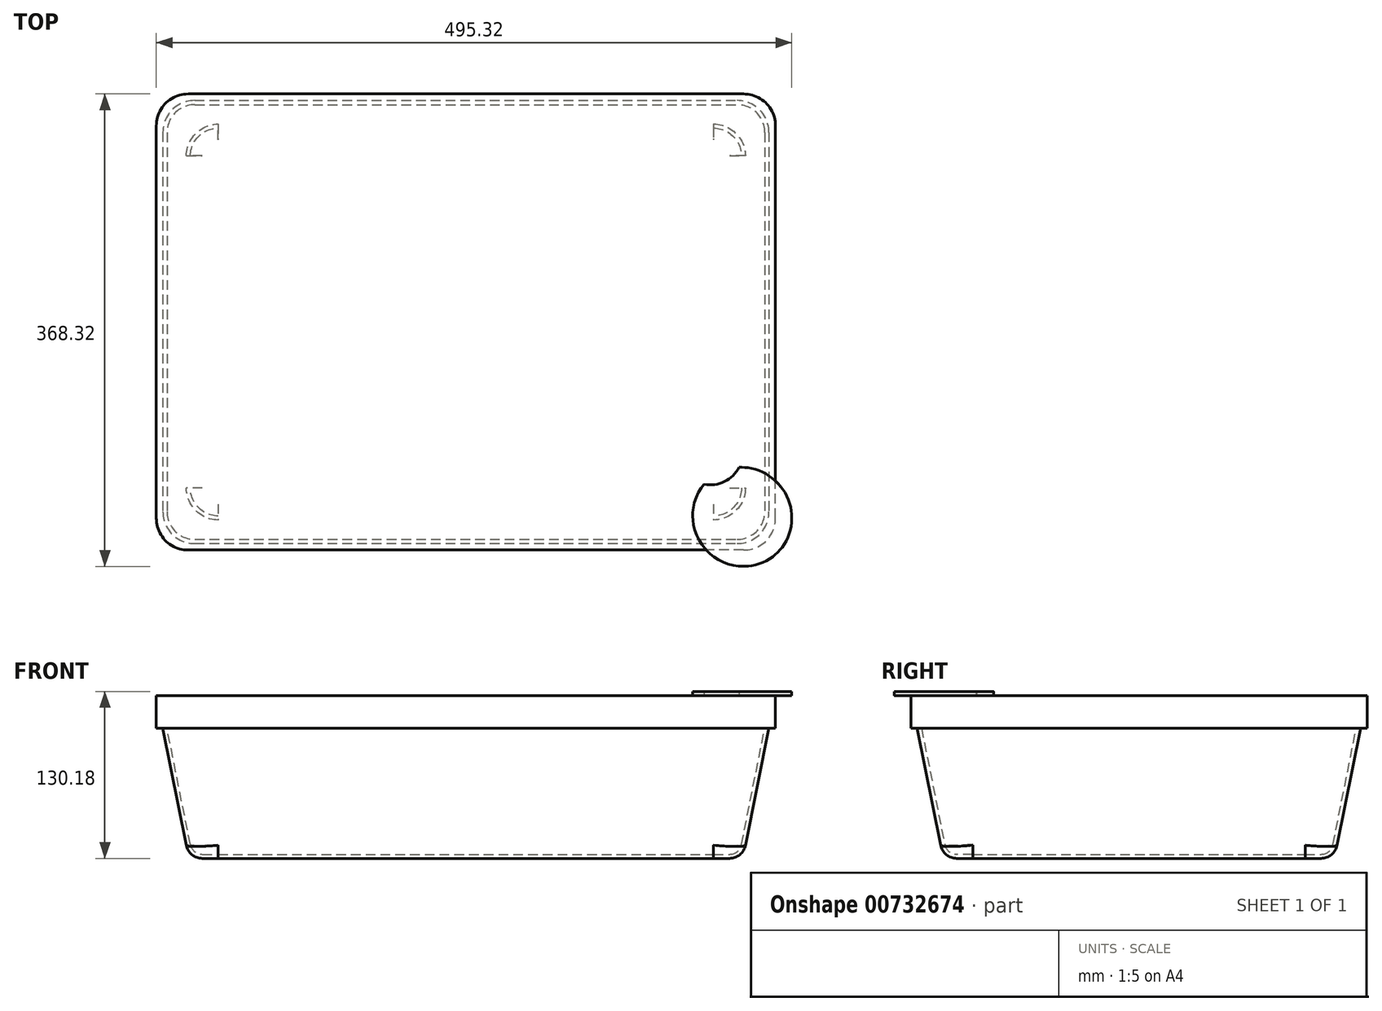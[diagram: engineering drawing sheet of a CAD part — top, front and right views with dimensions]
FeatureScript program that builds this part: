
annotation { "Feature Type Name" : "Feature", "Feature Type Description" : "" }
export const myFeature = defineFeature(function(context is Context, id is Id, definition is map)
    precondition{}
    {
        {
            var Q0;
            Q0=qCreatedBy(makeId("Top.planeOp"),FACE);
            var sketch = newSketch(context, id + "F0", { "sketchPlane" : qUnion([Q0])});
            skLineSegment(sketch, "E0.bottom", {"start": v(-241.3, 177.8) * mm, "end": v(241.3, 177.8) * mm});
            skLineSegment(sketch, "E0.top", {"start": v(-241.3, -177.8) * mm, "end": v(241.3, -177.8) * mm});
            skLineSegment(sketch, "E0.left", {"start": v(-241.3, 177.8) * mm, "end": v(-241.3, -177.8) * mm});
            skLineSegment(sketch, "E0.right", {"start": v(241.3, 177.8) * mm, "end": v(241.3, -177.8) * mm});
            skPoint(sketch, "E0.middle", {"position": v(0, 0) * mm});
            skSolve(sketch);
        }
        {
            var Q0;
            Q0=qCreatedBy(makeId("Top.planeOp"),FACE);
            cPlane(context, id + "F1", {"entities" : qUnion([Q0]), "cplaneType" : CPlaneType.OFFSET, "offset" : 127 * mm, "oppositeDirection" : true, "width" : 152.4 * mm, "height" : 152.4 * mm});
        }
        {
            var Q0;
            Q0=qCreatedBy(id+"F1.planeOp",FACE);
            var sketch = newSketch(context, id + "F2", { "sketchPlane" : qUnion([Q0])});
            skLineSegment(sketch, "E1.bottom", {"start": v(-215.9, 152.4) * mm, "end": v(215.9, 152.4) * mm});
            skLineSegment(sketch, "E1.top", {"start": v(-215.9, -152.4) * mm, "end": v(215.9, -152.4) * mm});
            skLineSegment(sketch, "E1.left", {"start": v(-215.9, 152.4) * mm, "end": v(-215.9, -152.4) * mm});
            skLineSegment(sketch, "E1.right", {"start": v(215.9, 152.4) * mm, "end": v(215.9, -152.4) * mm});
            skPoint(sketch, "E1.middle", {"position": v(0, 0) * mm});
            skSolve(sketch);
        }
        {
            var Q0;
            Q0=makeQuery(id+"F0.imprint","IMPRINT",FACE,{"disambiguationData":[TD([[makeQuery(id+"F0.imprint","IMPRINT",EDGE,{"derivedFrom":sQuery(id+"F0.wireOp",EDGE,"E0.bottom")}),-1.0]])]});
            var Q1;
            Q1=makeQuery(id+"F2.imprint","IMPRINT",FACE,{"disambiguationData":[TD([[makeQuery(id+"F2.imprint","IMPRINT",EDGE,{"derivedFrom":sQuery(id+"F2.wireOp",EDGE,"E1.bottom")}),-1.0]])]});
            loft(context, id + "F3", {"sheetProfilesArray" : [{ "sheetProfileEntities" : qUnion([Q0]) }, { "sheetProfileEntities" : qUnion([Q1]) }]});
        }
        {
            var Q0;
            Q0=makeQuery(id+"F3.opLoft","SWEPT_EDGE",EDGE,{"disambiguationData":[OSD([sQuery(id+"F0.wireOp",EDGE,"E0.top"),sQuery(id+"F0.wireOp",EDGE,"E0.left"),sQuery(id+"F2.wireOp",EDGE,"E1.top"),sQuery(id+"F2.wireOp",EDGE,"E1.left")])]});
            var Q1;
            Q1=makeQuery(id+"F3.opLoft","SWEPT_EDGE",EDGE,{"disambiguationData":[OSD([sQuery(id+"F0.wireOp",EDGE,"E0.top"),sQuery(id+"F0.wireOp",EDGE,"E0.right"),sQuery(id+"F2.wireOp",EDGE,"E1.top"),sQuery(id+"F2.wireOp",EDGE,"E1.right")])]});
            var Q2;
            Q2=makeQuery(id+"F3.opLoft","SWEPT_EDGE",EDGE,{"disambiguationData":[OSD([sQuery(id+"F0.wireOp",EDGE,"E0.bottom"),sQuery(id+"F0.wireOp",EDGE,"E0.right"),sQuery(id+"F2.wireOp",EDGE,"E1.bottom"),sQuery(id+"F2.wireOp",EDGE,"E1.right")])]});
            var Q3;
            Q3=makeQuery(id+"F3.opLoft","SWEPT_EDGE",EDGE,{"disambiguationData":[OSD([sQuery(id+"F0.wireOp",EDGE,"E0.bottom"),sQuery(id+"F0.wireOp",EDGE,"E0.left"),sQuery(id+"F2.wireOp",EDGE,"E1.bottom"),sQuery(id+"F2.wireOp",EDGE,"E1.left")])]});
            fillet(context, id + "F4", {"entities" : qUnion([Q0, Q1, Q2, Q3]), "radius" : 25.4 * mm, "tangentPropagation" : true, "allowEdgeOverflow" : false});
        }
        {
            var Q0;
            Q0=makeQuery(id+"F3.opLoft","CAP_FACE",FACE,{"disambiguationData":[OSD([makeQuery(id+"F2.imprint","IMPRINT",FACE,{"disambiguationData":[TD([[makeQuery(id+"F2.imprint","IMPRINT",EDGE,{"derivedFrom":sQuery(id+"F2.wireOp",EDGE,"E1.bottom")}),-1.0]])]})])],"isStart":true});
            fillet(context, id + "F5", {"entities" : qUnion([Q0]), "radius" : 12.7 * mm, "tangentPropagation" : true, "allowEdgeOverflow" : false});
        }
        {
            var Q0;
            Q0=makeQuery(id+"F3.opLoft","CAP_FACE",FACE,{"disambiguationData":[OSD([makeQuery(id+"F0.imprint","IMPRINT",FACE,{"disambiguationData":[TD([[makeQuery(id+"F0.imprint","IMPRINT",EDGE,{"derivedFrom":sQuery(id+"F0.wireOp",EDGE,"E0.bottom")}),-1.0]])]})])],"isStart":true});
            shell(context, id + "F6", {"entities" : qUnion([Q0]), "thickness" : 3.17 * mm});
        }
        {
            var Q0;
            Q0=qCreatedBy(makeId("Top.planeOp"),FACE);
            var sketch = newSketch(context, id + "F7", { "sketchPlane" : qUnion([Q0])});
            skLineSegment(sketch, "E2.0.0", {"start": v(-241.3, -152.9) * mm, "end": v(-241.3, 152.9) * mm});
            skEllipticalArc(sketch, "E2.0.1", {});
            skLineSegment(sketch, "E2.0.2", {"start": v(216.4, -177.8) * mm, "end": v(-216.4, -177.8) * mm});
            skEllipticalArc(sketch, "E2.0.3", {});
            skLineSegment(sketch, "E2.0.4", {"start": v(241.3, -152.9) * mm, "end": v(241.3, 152.9) * mm});
            skEllipticalArc(sketch, "E2.0.5", {});
            skLineSegment(sketch, "E2.0.6", {"start": v(216.4, 177.8) * mm, "end": v(-216.4, 177.8) * mm});
            skEllipticalArc(sketch, "E2.0.7", {});
            skFitSpline(sketch, "E3.0", {"points": [v(-186.42, -125.63) * mm, v(-187.74, -124.24) * mm, v(-189.13, -122.92) * mm, v(-191.06, -121.27) * mm, v(-193.62, -119.4) * mm, v(-196.88, -117.49) * mm, v(-200.3, -115.92) * mm, v(-203.87, -114.7) * mm, v(-207.55, -113.85) * mm, v(-210.69, -113.44) * mm, v(-213.23, -113.3) * mm, v(-215.14, -113.29) * mm, v(-217.06, -113.37) * mm, v(-219.59, -113.6) * mm, v(-222.7, -114.13) * mm, v(-226.36, -115.12) * mm, v(-229.89, -116.44) * mm, v(-233.28, -118.1) * mm, v(-236.5, -120.06) * mm, v(-239.04, -121.96) * mm, v(-240.96, -123.62) * mm, v(-242.35, -124.95) * mm, v(-243.67, -126.33) * mm, v(-245.34, -128.26) * mm, v(-247.23, -130.79) * mm, v(-249.2, -134.02) * mm, v(-250.85, -137.4) * mm, v(-252.18, -140.94) * mm, v(-253.16, -144.58) * mm, v(-253.69, -147.7) * mm, v(-253.92, -150.24) * mm, v(-254, -152.15) * mm, v(-254, -154.07) * mm, v(-253.86, -156.6) * mm, v(-253.45, -159.74) * mm, v(-252.59, -163.42) * mm, v(-251.37, -166.99) * mm, v(-249.8, -170.42) * mm, v(-247.9, -173.68) * mm, v(-246.03, -176.23) * mm, v(-244.37, -178.16) * mm, v(-243.05, -179.55) * mm, v(-241.66, -180.87) * mm, v(-239.73, -182.53) * mm, v(-237.18, -184.4) * mm, v(-233.92, -186.3) * mm, v(-230.49, -187.87) * mm, v(-226.92, -189.09) * mm, v(-223.24, -189.95) * mm, v(-220.1, -190.36) * mm, v(-217.57, -190.5) * mm, v(-215.65, -190.5) * mm, v(-213.74, -190.42) * mm, v(-211.2, -190.19) * mm, v(-208.08, -189.66) * mm, v(-204.44, -188.68) * mm, v(-200.9, -187.35) * mm, v(-197.52, -185.7) * mm, v(-194.29, -183.73) * mm, v(-191.76, -181.84) * mm, v(-189.83, -180.17) * mm, v(-188.45, -178.85) * mm, v(-187.12, -177.46) * mm, v(-185.46, -175.54) * mm, v(-183.56, -173) * mm, v(-181.6, -169.78) * mm, v(-179.94, -166.39) * mm, v(-178.62, -162.86) * mm, v(-177.63, -159.2) * mm, v(-177.1, -156.09) * mm, v(-176.87, -153.56) * mm, v(-176.79, -151.64) * mm, v(-176.8, -149.73) * mm, v(-176.94, -147.19) * mm, v(-177.35, -144.05) * mm, v(-178.2, -140.37) * mm, v(-179.42, -136.8) * mm, v(-180.99, -133.38) * mm, v(-182.9, -130.12) * mm, v(-184.77, -127.56) * mm, v(-186.42, -125.63) * mm, v(-187.74, -124.24) * mm, v(-189.13, -122.92) * mm]});
            skLineSegment(sketch, "E3.1", {"start": v(216.4, -190.5) * mm, "end": v(-216.4, -190.5) * mm});
            skLineSegment(sketch, "E3.2", {"start": v(-254, -152.9) * mm, "end": v(-254, 152.9) * mm});
            skFitSpline(sketch, "E3.3", {"points": [v(241.66, -180.87) * mm, v(243.05, -179.55) * mm, v(244.37, -178.16) * mm, v(246.03, -176.23) * mm, v(247.9, -173.68) * mm, v(249.8, -170.42) * mm, v(251.37, -166.99) * mm, v(252.59, -163.42) * mm, v(253.45, -159.74) * mm, v(253.86, -156.6) * mm, v(254, -154.07) * mm, v(254, -152.15) * mm, v(253.92, -150.24) * mm, v(253.69, -147.7) * mm, v(253.16, -144.58) * mm, v(252.18, -140.94) * mm, v(250.85, -137.4) * mm, v(249.2, -134.02) * mm, v(247.23, -130.79) * mm, v(245.34, -128.26) * mm, v(243.67, -126.33) * mm, v(242.35, -124.95) * mm, v(240.96, -123.62) * mm, v(239.04, -121.96) * mm, v(236.5, -120.06) * mm, v(233.28, -118.1) * mm, v(229.89, -116.44) * mm, v(226.36, -115.12) * mm, v(222.7, -114.13) * mm, v(219.59, -113.6) * mm, v(217.06, -113.37) * mm, v(215.14, -113.29) * mm, v(213.23, -113.3) * mm, v(210.69, -113.44) * mm, v(207.55, -113.85) * mm, v(203.87, -114.7) * mm, v(200.3, -115.92) * mm, v(196.88, -117.49) * mm, v(193.62, -119.4) * mm, v(191.06, -121.27) * mm, v(189.13, -122.92) * mm, v(187.74, -124.24) * mm, v(186.42, -125.63) * mm, v(184.77, -127.56) * mm, v(182.9, -130.12) * mm, v(180.99, -133.38) * mm, v(179.42, -136.8) * mm, v(178.2, -140.37) * mm, v(177.35, -144.05) * mm, v(176.94, -147.19) * mm, v(176.8, -149.73) * mm, v(176.79, -151.64) * mm, v(176.87, -153.56) * mm, v(177.1, -156.09) * mm, v(177.63, -159.2) * mm, v(178.62, -162.86) * mm, v(179.94, -166.39) * mm, v(181.6, -169.78) * mm, v(183.56, -173) * mm, v(185.46, -175.54) * mm, v(187.12, -177.46) * mm, v(188.45, -178.85) * mm, v(189.83, -180.17) * mm, v(191.76, -181.84) * mm, v(194.29, -183.73) * mm, v(197.52, -185.7) * mm, v(200.9, -187.35) * mm, v(204.44, -188.68) * mm, v(208.08, -189.66) * mm, v(211.2, -190.19) * mm, v(213.74, -190.42) * mm, v(215.65, -190.5) * mm, v(217.57, -190.5) * mm, v(220.1, -190.36) * mm, v(223.24, -189.95) * mm, v(226.92, -189.09) * mm, v(230.49, -187.87) * mm, v(233.92, -186.3) * mm, v(237.18, -184.4) * mm, v(239.73, -182.53) * mm, v(241.66, -180.87) * mm, v(243.05, -179.55) * mm, v(244.37, -178.16) * mm]});
            skFitSpline(sketch, "E3.4", {"points": [v(-241.66, 180.87) * mm, v(-243.05, 179.55) * mm, v(-244.37, 178.16) * mm, v(-246.03, 176.23) * mm, v(-247.9, 173.68) * mm, v(-249.8, 170.42) * mm, v(-251.37, 166.99) * mm, v(-252.59, 163.42) * mm, v(-253.45, 159.74) * mm, v(-253.86, 156.6) * mm, v(-254, 154.07) * mm, v(-254, 152.15) * mm, v(-253.92, 150.24) * mm, v(-253.69, 147.7) * mm, v(-253.16, 144.58) * mm, v(-252.18, 140.94) * mm, v(-250.85, 137.4) * mm, v(-249.2, 134.02) * mm, v(-247.23, 130.79) * mm, v(-245.34, 128.26) * mm, v(-243.67, 126.33) * mm, v(-242.35, 124.95) * mm, v(-240.96, 123.62) * mm, v(-239.04, 121.96) * mm, v(-236.5, 120.06) * mm, v(-233.28, 118.1) * mm, v(-229.89, 116.44) * mm, v(-226.36, 115.12) * mm, v(-222.7, 114.13) * mm, v(-219.59, 113.6) * mm, v(-217.06, 113.37) * mm, v(-215.14, 113.29) * mm, v(-213.23, 113.3) * mm, v(-210.69, 113.44) * mm, v(-207.55, 113.85) * mm, v(-203.87, 114.7) * mm, v(-200.3, 115.92) * mm, v(-196.88, 117.49) * mm, v(-193.62, 119.4) * mm, v(-191.06, 121.27) * mm, v(-189.13, 122.92) * mm, v(-187.74, 124.24) * mm, v(-186.42, 125.63) * mm, v(-184.77, 127.56) * mm, v(-182.9, 130.12) * mm, v(-180.99, 133.38) * mm, v(-179.42, 136.8) * mm, v(-178.2, 140.37) * mm, v(-177.35, 144.05) * mm, v(-176.94, 147.19) * mm, v(-176.8, 149.73) * mm, v(-176.79, 151.64) * mm, v(-176.87, 153.56) * mm, v(-177.1, 156.09) * mm, v(-177.63, 159.2) * mm, v(-178.62, 162.86) * mm, v(-179.94, 166.39) * mm, v(-181.6, 169.78) * mm, v(-183.56, 173) * mm, v(-185.46, 175.54) * mm, v(-187.12, 177.46) * mm, v(-188.45, 178.85) * mm, v(-189.83, 180.17) * mm, v(-191.76, 181.84) * mm, v(-194.29, 183.73) * mm, v(-197.52, 185.7) * mm, v(-200.9, 187.35) * mm, v(-204.44, 188.68) * mm, v(-208.08, 189.66) * mm, v(-211.2, 190.19) * mm, v(-213.74, 190.42) * mm, v(-215.65, 190.5) * mm, v(-217.57, 190.5) * mm, v(-220.1, 190.36) * mm, v(-223.24, 189.95) * mm, v(-226.92, 189.09) * mm, v(-230.49, 187.87) * mm, v(-233.92, 186.3) * mm, v(-237.18, 184.4) * mm, v(-239.73, 182.53) * mm, v(-241.66, 180.87) * mm, v(-243.05, 179.55) * mm, v(-244.37, 178.16) * mm]});
            skLineSegment(sketch, "E3.5", {"start": v(216.4, 190.5) * mm, "end": v(-216.4, 190.5) * mm});
            skFitSpline(sketch, "E3.6", {"points": [v(186.42, 125.63) * mm, v(187.74, 124.24) * mm, v(189.13, 122.92) * mm, v(191.06, 121.27) * mm, v(193.62, 119.4) * mm, v(196.88, 117.49) * mm, v(200.3, 115.92) * mm, v(203.87, 114.7) * mm, v(207.55, 113.85) * mm, v(210.69, 113.44) * mm, v(213.23, 113.3) * mm, v(215.14, 113.29) * mm, v(217.06, 113.37) * mm, v(219.59, 113.6) * mm, v(222.7, 114.13) * mm, v(226.36, 115.12) * mm, v(229.89, 116.44) * mm, v(233.28, 118.1) * mm, v(236.5, 120.06) * mm, v(239.04, 121.96) * mm, v(240.96, 123.62) * mm, v(242.35, 124.95) * mm, v(243.67, 126.33) * mm, v(245.34, 128.26) * mm, v(247.23, 130.79) * mm, v(249.2, 134.02) * mm, v(250.85, 137.4) * mm, v(252.18, 140.94) * mm, v(253.16, 144.58) * mm, v(253.69, 147.7) * mm, v(253.92, 150.24) * mm, v(254, 152.15) * mm, v(254, 154.07) * mm, v(253.86, 156.6) * mm, v(253.45, 159.74) * mm, v(252.59, 163.42) * mm, v(251.37, 166.99) * mm, v(249.8, 170.42) * mm, v(247.9, 173.68) * mm, v(246.03, 176.23) * mm, v(244.37, 178.16) * mm, v(243.05, 179.55) * mm, v(241.66, 180.87) * mm, v(239.73, 182.53) * mm, v(237.18, 184.4) * mm, v(233.92, 186.3) * mm, v(230.49, 187.87) * mm, v(226.92, 189.09) * mm, v(223.24, 189.95) * mm, v(220.1, 190.36) * mm, v(217.57, 190.5) * mm, v(215.65, 190.5) * mm, v(213.74, 190.42) * mm, v(211.2, 190.19) * mm, v(208.08, 189.66) * mm, v(204.44, 188.68) * mm, v(200.9, 187.35) * mm, v(197.52, 185.7) * mm, v(194.29, 183.73) * mm, v(191.76, 181.84) * mm, v(189.83, 180.17) * mm, v(188.45, 178.85) * mm, v(187.12, 177.46) * mm, v(185.46, 175.54) * mm, v(183.56, 173) * mm, v(181.6, 169.78) * mm, v(179.94, 166.39) * mm, v(178.62, 162.86) * mm, v(177.63, 159.2) * mm, v(177.1, 156.09) * mm, v(176.87, 153.56) * mm, v(176.79, 151.64) * mm, v(176.8, 149.73) * mm, v(176.94, 147.19) * mm, v(177.35, 144.05) * mm, v(178.2, 140.37) * mm, v(179.42, 136.8) * mm, v(180.99, 133.38) * mm, v(182.9, 130.12) * mm, v(184.77, 127.56) * mm, v(186.42, 125.63) * mm, v(187.74, 124.24) * mm, v(189.13, 122.92) * mm]});
            skLineSegment(sketch, "E3.7", {"start": v(254, -152.9) * mm, "end": v(254, 152.9) * mm});
            const initialGuessF7  = {"E2.0.1": [-0.21539698087094875, -0.15189698087094863, 0.7071067811865485, 0.7071067811865468, 0.026396454307349694, 0.0254, 2.3754300038960103, 3.907755303283578], "E2.0.3": [0.2153969808709486, -0.15189698087094866, 0.7071067811865475, -0.7071067811865476, 0.026396454307349694, 0.0254, 5.517022657485803, 0.7661626496937839], "E2.0.5": [0.21539698087094866, 0.1518969808709486, -0.7071067811865482, -0.7071067811865468, 0.026396454307349694, 0.0254, 2.3754300038960103, 3.9077553032835777], "E2.0.7": [-0.21539698087094872, 0.1518969808709486, -0.7071067811865489, 0.7071067811865461, 0.026396454307349694, 0.0254, 5.517022657485801, 0.766162649693783]};
            skSetInitialGuess(sketch, initialGuessF7);
            skSolve(sketch);
        }
        {
            var Q0;
            Q0 = qSketchRegion(id + "F7", true);
            extrude(context, id + "F8", {"entities" : qUnion([Q0]), "oppositeDirection" : true, "depth" : 25.4 * mm, "offsetDistance" : 25.4 * mm});
        }
        {
            var Q0;
            Q0=qCreatedBy(makeId("Top.planeOp"),FACE);
            var sketch = newSketch(context, id + "F9", { "sketchPlane" : qUnion([Q0])});
            skFitSpline(sketch, "E4.0.0", {"points": [v(243.04, -179.54) * mm, v(243.5, -179.1) * mm, v(244.37, -178.16) * mm, v(246.03, -176.23) * mm, v(247.9, -173.68) * mm, v(249.8, -170.42) * mm, v(251.37, -166.99) * mm, v(252.59, -163.42) * mm, v(253.45, -159.74) * mm, v(253.86, -156.6) * mm, v(254, -154.07) * mm, v(254, -152.15) * mm, v(253.92, -150.24) * mm, v(253.69, -147.7) * mm, v(253.16, -144.58) * mm, v(252.18, -140.94) * mm, v(250.85, -137.4) * mm, v(249.2, -134.02) * mm, v(247.23, -130.79) * mm, v(245.34, -128.26) * mm, v(243.67, -126.33) * mm, v(242.35, -124.95) * mm, v(240.96, -123.62) * mm, v(239.04, -121.96) * mm, v(236.5, -120.06) * mm, v(233.28, -118.1) * mm, v(229.89, -116.44) * mm, v(226.36, -115.12) * mm, v(222.7, -114.13) * mm, v(219.59, -113.6) * mm, v(217.06, -113.37) * mm, v(215.14, -113.29) * mm, v(213.23, -113.3) * mm, v(210.69, -113.44) * mm, v(207.55, -113.85) * mm, v(203.87, -114.7) * mm, v(200.3, -115.92) * mm, v(196.88, -117.49) * mm, v(193.62, -119.4) * mm, v(191.06, -121.27) * mm, v(189.13, -122.92) * mm, v(187.74, -124.24) * mm, v(186.42, -125.63) * mm, v(184.77, -127.56) * mm, v(182.9, -130.12) * mm, v(180.99, -133.38) * mm, v(179.42, -136.8) * mm, v(178.2, -140.37) * mm, v(177.35, -144.05) * mm, v(176.94, -147.19) * mm, v(176.8, -149.73) * mm, v(176.79, -151.64) * mm, v(176.87, -153.56) * mm, v(177.1, -156.09) * mm, v(177.63, -159.2) * mm, v(178.62, -162.86) * mm, v(179.94, -166.39) * mm, v(181.6, -169.78) * mm, v(183.56, -173) * mm, v(185.46, -175.54) * mm, v(187.12, -177.46) * mm, v(188.45, -178.85) * mm, v(189.83, -180.17) * mm, v(191.76, -181.84) * mm, v(194.29, -183.73) * mm, v(197.52, -185.7) * mm, v(200.9, -187.35) * mm, v(204.44, -188.68) * mm, v(208.08, -189.66) * mm, v(211.2, -190.19) * mm, v(213.74, -190.42) * mm, v(215.65, -190.5) * mm, v(217.57, -190.5) * mm, v(220.1, -190.36) * mm, v(223.24, -189.95) * mm, v(226.92, -189.09) * mm, v(230.49, -187.87) * mm, v(233.92, -186.3) * mm, v(237.18, -184.4) * mm, v(239.73, -182.53) * mm, v(241.66, -180.87) * mm, v(242.6, -180) * mm, v(243.04, -179.54) * mm]});
            skLineSegment(sketch, "E4.0.1", {"start": v(254, -152.9) * mm, "end": v(254, 152.9) * mm});
            skFitSpline(sketch, "E4.0.2", {"points": [v(187.75, 124.25) * mm, v(188.2, 123.8) * mm, v(189.13, 122.92) * mm, v(191.06, 121.27) * mm, v(193.62, 119.4) * mm, v(196.88, 117.49) * mm, v(200.3, 115.92) * mm, v(203.87, 114.7) * mm, v(207.55, 113.85) * mm, v(210.69, 113.44) * mm, v(213.23, 113.3) * mm, v(215.14, 113.29) * mm, v(217.06, 113.37) * mm, v(219.59, 113.6) * mm, v(222.7, 114.13) * mm, v(226.36, 115.12) * mm, v(229.89, 116.44) * mm, v(233.28, 118.1) * mm, v(236.5, 120.06) * mm, v(239.04, 121.96) * mm, v(240.96, 123.62) * mm, v(242.35, 124.95) * mm, v(243.67, 126.33) * mm, v(245.34, 128.26) * mm, v(247.23, 130.79) * mm, v(249.2, 134.02) * mm, v(250.85, 137.4) * mm, v(252.18, 140.94) * mm, v(253.16, 144.58) * mm, v(253.69, 147.7) * mm, v(253.92, 150.24) * mm, v(254, 152.15) * mm, v(254, 154.07) * mm, v(253.86, 156.6) * mm, v(253.45, 159.74) * mm, v(252.59, 163.42) * mm, v(251.37, 166.99) * mm, v(249.8, 170.42) * mm, v(247.9, 173.68) * mm, v(246.03, 176.23) * mm, v(244.37, 178.16) * mm, v(243.05, 179.55) * mm, v(241.66, 180.87) * mm, v(239.73, 182.53) * mm, v(237.18, 184.4) * mm, v(233.92, 186.3) * mm, v(230.49, 187.87) * mm, v(226.92, 189.09) * mm, v(223.24, 189.95) * mm, v(220.1, 190.36) * mm, v(217.57, 190.5) * mm, v(215.65, 190.5) * mm, v(213.74, 190.42) * mm, v(211.2, 190.19) * mm, v(208.08, 189.66) * mm, v(204.44, 188.68) * mm, v(200.9, 187.35) * mm, v(197.52, 185.7) * mm, v(194.29, 183.73) * mm, v(191.76, 181.84) * mm, v(189.83, 180.17) * mm, v(188.45, 178.85) * mm, v(187.12, 177.46) * mm, v(185.46, 175.54) * mm, v(183.56, 173) * mm, v(181.6, 169.78) * mm, v(179.94, 166.39) * mm, v(178.62, 162.86) * mm, v(177.63, 159.2) * mm, v(177.1, 156.09) * mm, v(176.87, 153.56) * mm, v(176.79, 151.64) * mm, v(176.8, 149.73) * mm, v(176.94, 147.19) * mm, v(177.35, 144.05) * mm, v(178.2, 140.37) * mm, v(179.42, 136.8) * mm, v(180.99, 133.38) * mm, v(182.9, 130.12) * mm, v(184.77, 127.56) * mm, v(186.42, 125.63) * mm, v(187.3, 124.7) * mm, v(187.75, 124.25) * mm]});
            skLineSegment(sketch, "E4.0.3", {"start": v(216.4, 190.5) * mm, "end": v(-216.4, 190.5) * mm});
            skFitSpline(sketch, "E4.0.4", {"points": [v(-243.04, 179.54) * mm, v(-243.5, 179.1) * mm, v(-244.37, 178.16) * mm, v(-246.03, 176.23) * mm, v(-247.9, 173.68) * mm, v(-249.8, 170.42) * mm, v(-251.37, 166.99) * mm, v(-252.59, 163.42) * mm, v(-253.45, 159.74) * mm, v(-253.86, 156.6) * mm, v(-254, 154.07) * mm, v(-254, 152.15) * mm, v(-253.92, 150.24) * mm, v(-253.69, 147.7) * mm, v(-253.16, 144.58) * mm, v(-252.18, 140.94) * mm, v(-250.85, 137.4) * mm, v(-249.2, 134.02) * mm, v(-247.23, 130.79) * mm, v(-245.34, 128.26) * mm, v(-243.67, 126.33) * mm, v(-242.35, 124.95) * mm, v(-240.96, 123.62) * mm, v(-239.04, 121.96) * mm, v(-236.5, 120.06) * mm, v(-233.28, 118.1) * mm, v(-229.89, 116.44) * mm, v(-226.36, 115.12) * mm, v(-222.7, 114.13) * mm, v(-219.59, 113.6) * mm, v(-217.06, 113.37) * mm, v(-215.14, 113.29) * mm, v(-213.23, 113.3) * mm, v(-210.69, 113.44) * mm, v(-207.55, 113.85) * mm, v(-203.87, 114.7) * mm, v(-200.3, 115.92) * mm, v(-196.88, 117.49) * mm, v(-193.62, 119.4) * mm, v(-191.06, 121.27) * mm, v(-189.13, 122.92) * mm, v(-187.74, 124.24) * mm, v(-186.42, 125.63) * mm, v(-184.77, 127.56) * mm, v(-182.9, 130.12) * mm, v(-180.99, 133.38) * mm, v(-179.42, 136.8) * mm, v(-178.2, 140.37) * mm, v(-177.35, 144.05) * mm, v(-176.94, 147.19) * mm, v(-176.8, 149.73) * mm, v(-176.79, 151.64) * mm, v(-176.87, 153.56) * mm, v(-177.1, 156.09) * mm, v(-177.63, 159.2) * mm, v(-178.62, 162.86) * mm, v(-179.94, 166.39) * mm, v(-181.6, 169.78) * mm, v(-183.56, 173) * mm, v(-185.46, 175.54) * mm, v(-187.12, 177.46) * mm, v(-188.45, 178.85) * mm, v(-189.83, 180.17) * mm, v(-191.76, 181.84) * mm, v(-194.29, 183.73) * mm, v(-197.52, 185.7) * mm, v(-200.9, 187.35) * mm, v(-204.44, 188.68) * mm, v(-208.08, 189.66) * mm, v(-211.2, 190.19) * mm, v(-213.74, 190.42) * mm, v(-215.65, 190.5) * mm, v(-217.57, 190.5) * mm, v(-220.1, 190.36) * mm, v(-223.24, 189.95) * mm, v(-226.92, 189.09) * mm, v(-230.49, 187.87) * mm, v(-233.92, 186.3) * mm, v(-237.18, 184.4) * mm, v(-239.73, 182.53) * mm, v(-241.66, 180.87) * mm, v(-242.6, 180) * mm, v(-243.04, 179.54) * mm]});
            skLineSegment(sketch, "E4.0.5", {"start": v(-254, 152.9) * mm, "end": v(-254, -152.9) * mm});
            skFitSpline(sketch, "E4.0.6", {"points": [v(-187.75, -124.25) * mm, v(-188.2, -123.8) * mm, v(-189.13, -122.92) * mm, v(-191.06, -121.27) * mm, v(-193.62, -119.4) * mm, v(-196.88, -117.49) * mm, v(-200.3, -115.92) * mm, v(-203.87, -114.7) * mm, v(-207.55, -113.85) * mm, v(-210.69, -113.44) * mm, v(-213.23, -113.3) * mm, v(-215.14, -113.29) * mm, v(-217.06, -113.37) * mm, v(-219.59, -113.6) * mm, v(-222.7, -114.13) * mm, v(-226.36, -115.12) * mm, v(-229.89, -116.44) * mm, v(-233.28, -118.1) * mm, v(-236.5, -120.06) * mm, v(-239.04, -121.96) * mm, v(-240.96, -123.62) * mm, v(-242.35, -124.95) * mm, v(-243.67, -126.33) * mm, v(-245.34, -128.26) * mm, v(-247.23, -130.79) * mm, v(-249.2, -134.02) * mm, v(-250.85, -137.4) * mm, v(-252.18, -140.94) * mm, v(-253.16, -144.58) * mm, v(-253.69, -147.7) * mm, v(-253.92, -150.24) * mm, v(-254, -152.15) * mm, v(-254, -154.07) * mm, v(-253.86, -156.6) * mm, v(-253.45, -159.74) * mm, v(-252.59, -163.42) * mm, v(-251.37, -166.99) * mm, v(-249.8, -170.42) * mm, v(-247.9, -173.68) * mm, v(-246.03, -176.23) * mm, v(-244.37, -178.16) * mm, v(-243.05, -179.55) * mm, v(-241.66, -180.87) * mm, v(-239.73, -182.53) * mm, v(-237.18, -184.4) * mm, v(-233.92, -186.3) * mm, v(-230.49, -187.87) * mm, v(-226.92, -189.09) * mm, v(-223.24, -189.95) * mm, v(-220.1, -190.36) * mm, v(-217.57, -190.5) * mm, v(-215.65, -190.5) * mm, v(-213.74, -190.42) * mm, v(-211.2, -190.19) * mm, v(-208.08, -189.66) * mm, v(-204.44, -188.68) * mm, v(-200.9, -187.35) * mm, v(-197.52, -185.7) * mm, v(-194.29, -183.73) * mm, v(-191.76, -181.84) * mm, v(-189.83, -180.17) * mm, v(-188.45, -178.85) * mm, v(-187.12, -177.46) * mm, v(-185.46, -175.54) * mm, v(-183.56, -173) * mm, v(-181.6, -169.78) * mm, v(-179.94, -166.39) * mm, v(-178.62, -162.86) * mm, v(-177.63, -159.2) * mm, v(-177.1, -156.09) * mm, v(-176.87, -153.56) * mm, v(-176.79, -151.64) * mm, v(-176.8, -149.73) * mm, v(-176.94, -147.19) * mm, v(-177.35, -144.05) * mm, v(-178.2, -140.37) * mm, v(-179.42, -136.8) * mm, v(-180.99, -133.38) * mm, v(-182.9, -130.12) * mm, v(-184.77, -127.56) * mm, v(-186.42, -125.63) * mm, v(-187.3, -124.7) * mm, v(-187.75, -124.25) * mm]});
            skLineSegment(sketch, "E4.0.7", {"start": v(-216.4, -190.5) * mm, "end": v(216.4, -190.5) * mm});
            skCircle(sketch, "E5", {"center": v(-190.5, 101.6) * mm, "radius": 25.4 * mm});
            skCircle(sketch, "E6", {"center": v(-190.5, -101.6) * mm, "radius": 25.4 * mm});
            skLineSegment(sketch, "E7", {"start": v(0, 190.5) * mm, "end": v(0, -190.5) * mm, "construction": true});
            skCircle(sketch, "E8.1.0.0", {"center": v(0, 101.6) * mm, "radius": 25.4 * mm});
            skCircle(sketch, "E8.1.0.1", {"center": v(0, -101.6) * mm, "radius": 25.4 * mm});
            skCircle(sketch, "E8.2.0.0", {"center": v(190.5, 101.6) * mm, "radius": 25.4 * mm});
            skCircle(sketch, "E8.2.0.1", {"center": v(190.5, -101.6) * mm, "radius": 25.4 * mm});
            skLineSegment(sketch, "E8.direction1", {"start": v(-190.5, 101.6) * mm, "end": v(0, 101.6) * mm, "construction": true});
            skSolve(sketch);
        }
        {
            var Q0;
            Q0=makeQuery(id+"F9.imprint","IMPRINT",FACE,{"disambiguationData":[TD([[makeQuery(id+"F9.imprint","IMPRINT",EDGE,{"derivedFrom":sQuery(id+"F9.wireOp",EDGE,"E4.0.0")}),1.0]])]});
            extrude(context, id + "F10", {"entities" : qUnion([Q0]), "operationType" : NewBodyOperationType.ADD, "depth" : 3.17 * mm, "offsetDistance" : 25.4 * mm});
        }
    });
